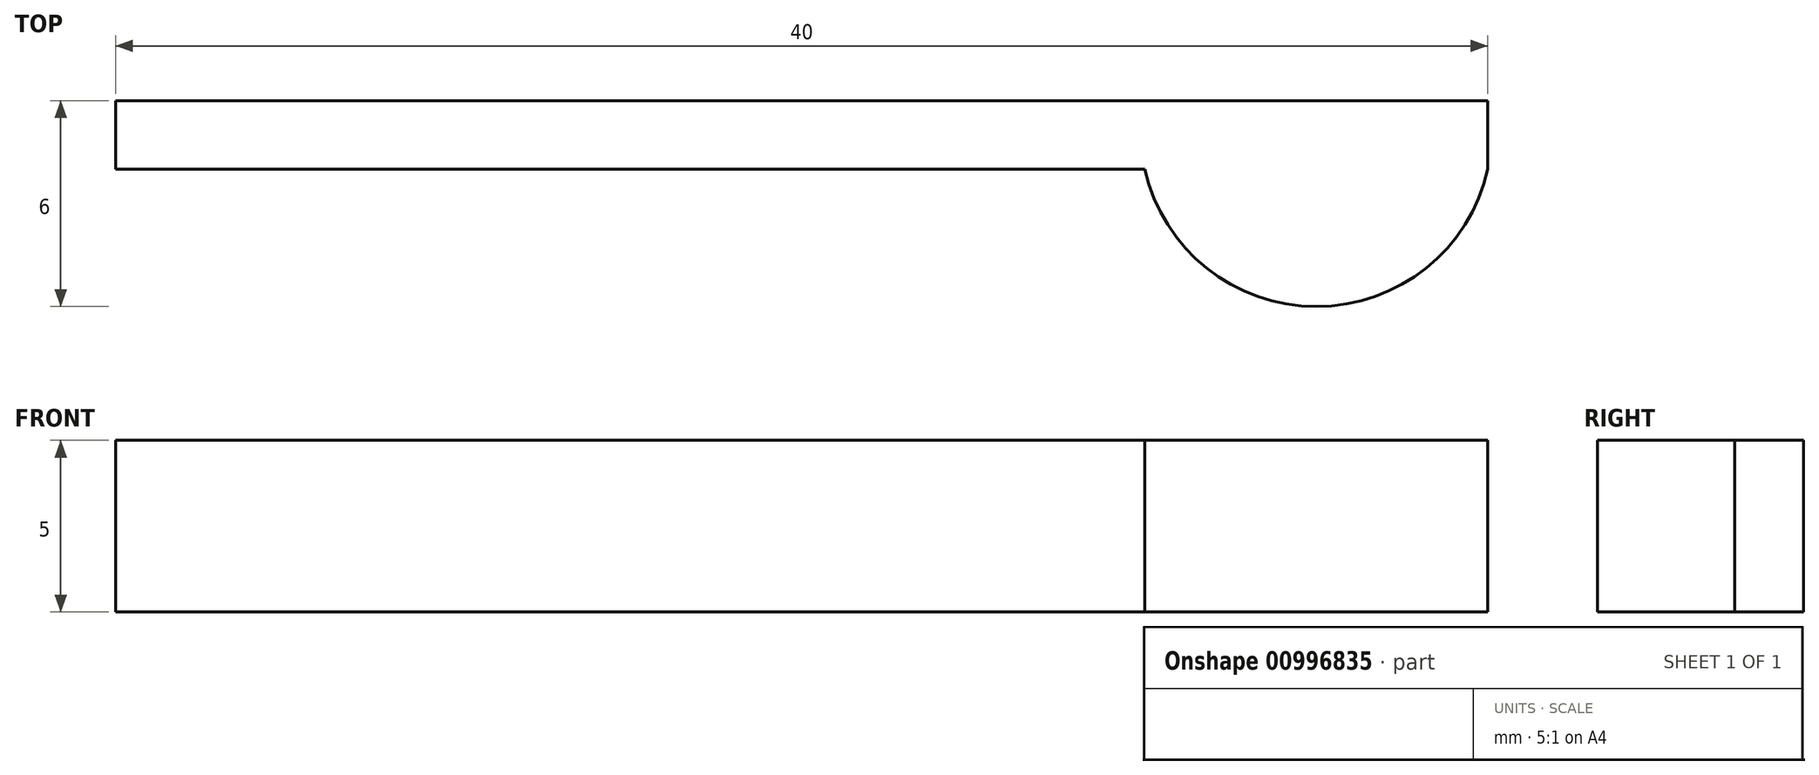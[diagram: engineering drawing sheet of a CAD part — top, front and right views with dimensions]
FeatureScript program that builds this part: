
annotation { "Feature Type Name" : "Feature", "Feature Type Description" : "" }
export const myFeature = defineFeature(function(context is Context, id is Id, definition is map)
    precondition{}
    {
        {
            var Q0;
            Q0=qCreatedBy(makeId("Top.planeOp"),FACE);
            var sketch = newSketch(context, id + "F0", { "sketchPlane" : qUnion([Q0])});
            skLineSegment(sketch, "E0.bottom", {"start": v(0, 0) * mm, "end": v(40, 0) * mm});
            skLineSegment(sketch, "E0.top", {"start": v(0, -2) * mm, "end": v(30, -2) * mm});
            skLineSegment(sketch, "E0.left", {"start": v(0, 0) * mm, "end": v(0, -2) * mm});
            skLineSegment(sketch, "E0.right", {"start": v(40, 0) * mm, "end": v(40, -2) * mm});
            skArc(sketch, "E1", {"start": v(30, -2) * mm, "mid": v(35, -6) * mm, "end": v(40, -2) * mm});
            skSolve(sketch);
        }
        {
            var Q0;
            Q0=makeQuery(id+"F0.imprint","IMPRINT",FACE,{"disambiguationData":[TD([[makeQuery(id+"F0.imprint","IMPRINT",EDGE,{"derivedFrom":sQuery(id+"F0.wireOp",EDGE,"E0.bottom")}),-1.0]])]});
            extrude(context, id + "F1", {"entities" : qUnion([Q0]), "depth" : 5 * mm, "offsetDistance" : 25 * mm});
        }
    });
